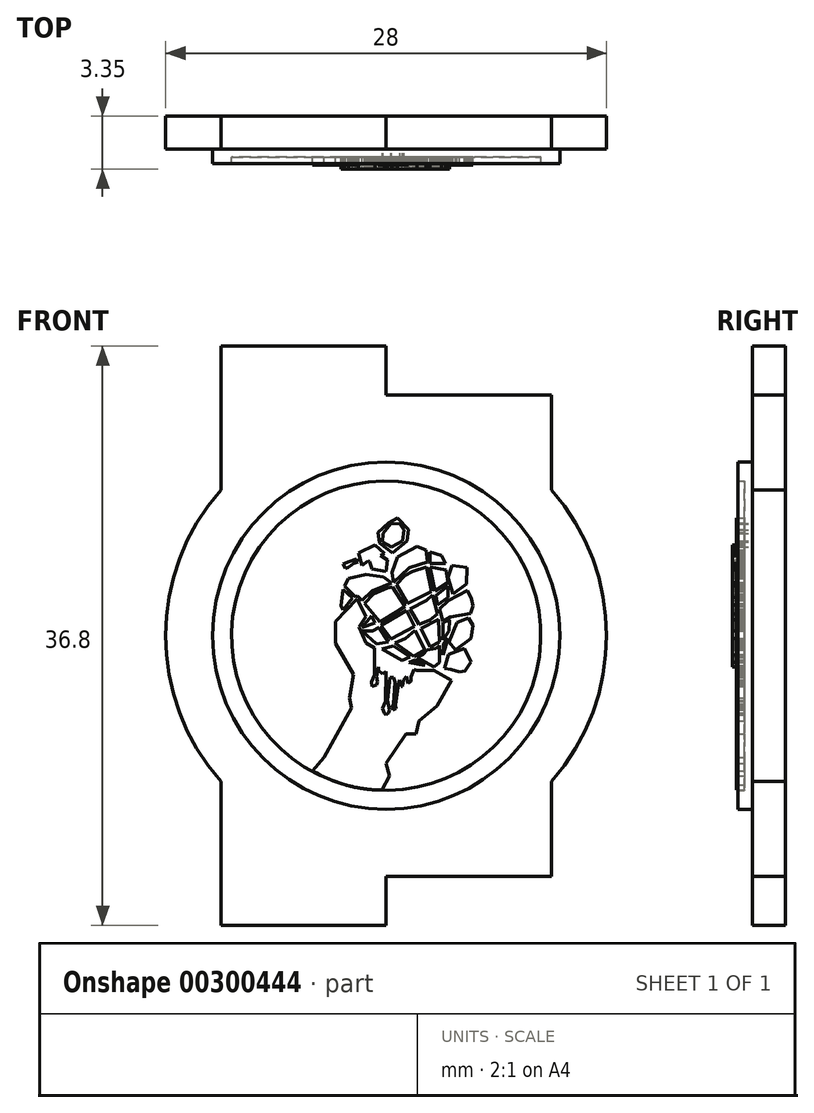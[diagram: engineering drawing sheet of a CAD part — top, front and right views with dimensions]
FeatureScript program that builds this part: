
annotation { "Feature Type Name" : "Feature", "Feature Type Description" : "" }
export const myFeature = defineFeature(function(context is Context, id is Id, definition is map)
    precondition{}
    {
        {
            var Q0;
            Q0=qCreatedBy(makeId("Front.planeOp"),FACE);
            var sketch = newSketch(context, id + "F0", { "sketchPlane" : qUnion([Q0])});
            skLineSegment(sketch, "E0", {"start": v(0, 0) * mm, "end": v(10.5, 0) * mm, "construction": true});
            skLineSegment(sketch, "E1", {"start": v(0, 0) * mm, "end": v(-10.5, 0) * mm, "construction": true});
            skLineSegment(sketch, "E2", {"start": v(0, 0) * mm, "end": v(0, -18.4) * mm, "construction": true});
            skLineSegment(sketch, "E3", {"start": v(0, 0) * mm, "end": v(0, 18.4) * mm, "construction": true});
            skArc(sketch, "E4", {"start": v(-10.5, 9.26) * mm, "mid": v(-14, 0) * mm, "end": v(-10.5, -9.26) * mm});
            skLineSegment(sketch, "E5", {"start": v(-10.5, 18.4) * mm, "end": v(-10.5, 9.26) * mm, "construction": true});
            skLineSegment(sketch, "E6.MirrorCS", {"start": v(10.5, 18.4) * mm, "end": v(10.5, -19.66) * mm, "construction": true});
            skLineSegment(sketch, "E7", {"start": v(0, 18.4) * mm, "end": v(-10.5, 18.4) * mm});
            skLineSegment(sketch, "E8", {"start": v(10.5, 0) * mm, "end": v(10.5, 15.3) * mm});
            skLineSegment(sketch, "E9", {"start": v(10.5, 15.3) * mm, "end": v(0, 15.3) * mm});
            skLineSegment(sketch, "E10", {"start": v(0, 15.3) * mm, "end": v(0, 18.4) * mm});
            skLineSegment(sketch, "E11", {"start": v(-10.5, 18.4) * mm, "end": v(-10.5, 9.26) * mm});
            skLineSegment(sketch, "E12.MirrorCS", {"start": v(-10.5, -18.4) * mm, "end": v(-10.5, -9.26) * mm});
            skLineSegment(sketch, "E13.MirrorCS", {"start": v(0, -18.4) * mm, "end": v(-10.5, -18.4) * mm});
            skLineSegment(sketch, "E14.MirrorCS", {"start": v(10.5, -15.3) * mm, "end": v(0, -15.3) * mm});
            skLineSegment(sketch, "E15.MirrorCS", {"start": v(10.5, -9.26) * mm, "end": v(10.5, -15.3) * mm});
            skPoint(sketch, "E16.orphan", {"position": v(-10.5, 0) * mm});
            skLineSegment(sketch, "E17.trimOffspring", {"start": v(-10.5, -9.26) * mm, "end": v(-10.5, -19.66) * mm, "construction": true});
            skPoint(sketch, "E18.orphan", {"position": v(10.5, 0) * mm});
            skArc(sketch, "E19.trimOffspring", {"start": v(10.5, -9.26) * mm, "mid": v(14, 0) * mm, "end": v(10.5, 9.26) * mm});
            skLineSegment(sketch, "E20", {"start": v(0, -15.3) * mm, "end": v(0, -18.4) * mm});
            skSolve(sketch);
        }
        {
            var Q0;
            Q0=makeQuery(id+"F0.imprint","IMPRINT",FACE,{"disambiguationData":[TD([[makeQuery(id+"F0.imprint","IMPRINT",EDGE,{"derivedFrom":sQuery(id+"F0.wireOp",EDGE,"E4")}),1.0]])]});
            var sketch = newSketch(context, id + "F1", { "sketchPlane" : qUnion([Q0])});
            skCircle(sketch, "E21", {"center": v(0, 0) * mm, "radius": 11.03 * mm});
            skCircle(sketch, "E22", {"center": v(0, 0) * mm, "radius": 9.82 * mm});
            skSolve(sketch);
        }
        {
            var Q0;
            Q0=makeQuery(id+"F0.imprint","IMPRINT",FACE,{"disambiguationData":[TD([[makeQuery(id+"F0.imprint","IMPRINT",EDGE,{"derivedFrom":sQuery(id+"F0.wireOp",EDGE,"E4")}),1.0]])]});
            extrude(context, id + "F2", {"entities" : qUnion([Q0]), "depth" : 2.1 * mm});
        }
        {
            var Q0;
            Q0 = qSketchRegion(id + "F1", true);
            extrude(context, id + "F3", {"entities" : qUnion([Q0]), "operationType" : NewBodyOperationType.ADD, "depth" : 3 * mm});
        }
        {
            var Q0;
            {var subQ0=sQuery(id+"F0.wireOp",EDGE,"E14.MirrorCS");var subQ1=sQuery(id+"F0.wireOp",EDGE,"E13.MirrorCS");var subQ2=sQuery(id+"F0.wireOp",EDGE,"E12.MirrorCS");var subQ3=sQuery(id+"F0.wireOp",EDGE,"E11");var subQ4=sQuery(id+"F0.wireOp",EDGE,"E10");var subQ5=sQuery(id+"F0.wireOp",EDGE,"E15.MirrorCS");var subQ6=sQuery(id+"F0.wireOp",EDGE,"E4");var subQ7=sQuery(id+"F0.wireOp",EDGE,"E9");var subQ8=sQuery(id+"F0.wireOp",EDGE,"E7");var subQ9=sQuery(id+"F0.wireOp",EDGE,"E8");var subQ10=sQuery(id+"F0.wireOp",EDGE,"E19.trimOffspring");var subQ11=sQuery(id+"F0.wireOp",EDGE,"E20");Q0=makeQuery(id+"F3.boolean.opBoolean","SPLIT",FACE,{"disambiguationData":[TD([makeQuery(id+"F2.opExtrude","SWEPT_FACE",FACE,{"disambiguationData":[OSD([subQ6])]})])],"derivedFrom":makeQuery(id+"F2.opExtrude","CAP_FACE",FACE,{"disambiguationData":[OSD([subQ6,subQ8,subQ9,subQ7,subQ4,subQ3,subQ2,subQ1,subQ0,subQ5,subQ10,subQ11])],"isStart":false})});}
            var sketch = newSketch(context, id + "F4", { "sketchPlane" : qUnion([Q0])});
            skLineSegment(sketch, "E23", {"start": v(-4.66, -8.58) * mm, "end": v(-3.94, -7.74) * mm});
            skLineSegment(sketch, "E24", {"start": v(-3.94, -7.74) * mm, "end": v(-2.2, -4.58) * mm});
            skLineSegment(sketch, "E25", {"start": v(-2.2, -4.58) * mm, "end": v(-2.34, -3.96) * mm});
            skLineSegment(sketch, "E26", {"start": v(-2.34, -3.96) * mm, "end": v(-2.07, -2.47) * mm});
            skLineSegment(sketch, "E27", {"start": v(-2.07, -2.47) * mm, "end": v(-3.23, -0.5) * mm});
            skLineSegment(sketch, "E28", {"start": v(-3.23, -0.5) * mm, "end": v(-3.23, 0.92) * mm});
            skLineSegment(sketch, "E29", {"start": v(-3.23, 0.92) * mm, "end": v(-1.84, 2.32) * mm});
            skLineSegment(sketch, "E30", {"start": v(-1.84, 2.32) * mm, "end": v(-1.27, 1.2) * mm});
            skLineSegment(sketch, "E31", {"start": v(-1.27, 1.2) * mm, "end": v(-1.72, 0.56) * mm});
            skLineSegment(sketch, "E32", {"start": v(-1.72, 0.56) * mm, "end": v(-1.29, -0.48) * mm});
            skLineSegment(sketch, "E33", {"start": v(-1.29, -0.48) * mm, "end": v(0.72, -1.63) * mm});
            skLineSegment(sketch, "E34", {"start": v(0.72, -1.63) * mm, "end": v(0.72, -2.33) * mm});
            skLineSegment(sketch, "E35", {"start": v(0.72, -2.33) * mm, "end": v(1.05, -1.92) * mm});
            skLineSegment(sketch, "E36", {"start": v(1.05, -1.92) * mm, "end": v(1.96, -2.21) * mm});
            skLineSegment(sketch, "E37", {"start": v(1.96, -2.21) * mm, "end": v(3.04, -2.21) * mm});
            skLineSegment(sketch, "E38", {"start": v(3.04, -2.21) * mm, "end": v(4.16, -2.85) * mm});
            skLineSegment(sketch, "E39", {"start": v(4.16, -2.85) * mm, "end": v(3.25, -4.47) * mm});
            skLineSegment(sketch, "E40", {"start": v(3.25, -4.47) * mm, "end": v(2.1, -5.42) * mm});
            skLineSegment(sketch, "E41", {"start": v(2.1, -5.42) * mm, "end": v(1.88, -6.23) * mm});
            skLineSegment(sketch, "E42", {"start": v(1.88, -6.23) * mm, "end": v(1.27, -6.23) * mm});
            skLineSegment(sketch, "E43", {"start": v(1.27, -6.23) * mm, "end": v(0, -8.11) * mm});
            skLineSegment(sketch, "E44", {"start": v(0, -8.11) * mm, "end": v(0.21, -8.92) * mm});
            skLineSegment(sketch, "E45", {"start": v(0.21, -8.92) * mm, "end": v(-0.25, -9.81) * mm});
            skArc(sketch, "E46", {"start": v(-4.66, -8.58) * mm, "mid": v(-2.54, -9.49) * mm, "end": v(-0.25, -9.81) * mm});
            skLineSegment(sketch, "E47", {"start": v(-3.23, 0.92) * mm, "end": v(-2.75, 2.95) * mm});
            skLineSegment(sketch, "E48", {"start": v(-2.75, 2.95) * mm, "end": v(-2.4, 3.64) * mm});
            skLineSegment(sketch, "E49", {"start": v(-2.4, 3.64) * mm, "end": v(-1.27, 3.89) * mm});
            skLineSegment(sketch, "E50", {"start": v(-1.27, 3.89) * mm, "end": v(-0.17, 3.73) * mm});
            skLineSegment(sketch, "E51", {"start": v(-0.17, 3.73) * mm, "end": v(0.35, 3.36) * mm});
            skLineSegment(sketch, "E52", {"start": v(0.35, 3.36) * mm, "end": v(-0.9, 2.86) * mm});
            skLineSegment(sketch, "E53", {"start": v(-0.9, 2.86) * mm, "end": v(-1.53, 2.23) * mm});
            skLineSegment(sketch, "E54", {"start": v(-1.53, 2.23) * mm, "end": v(-1.83, 2.53) * mm});
            skLineSegment(sketch, "E55", {"start": v(-1.83, 2.53) * mm, "end": v(-1.95, 2.47) * mm});
            skLineSegment(sketch, "E56", {"start": v(-1.95, 2.47) * mm, "end": v(-2.64, 3.16) * mm});
            skLineSegment(sketch, "E57", {"start": v(-2.75, 2.95) * mm, "end": v(-2.14, 2.4) * mm});
            skLineSegment(sketch, "E58", {"start": v(-2.14, 2.4) * mm, "end": v(-2.75, 1.64) * mm});
            skLineSegment(sketch, "E59", {"start": v(-2.75, 1.64) * mm, "end": v(-2.87, 1.89) * mm});
            skLineSegment(sketch, "E60", {"start": v(-2.87, 1.89) * mm, "end": v(-2.75, 2.95) * mm});
            skLineSegment(sketch, "E61", {"start": v(0.48, 3.4) * mm, "end": v(0.36, 4) * mm});
            skLineSegment(sketch, "E62", {"start": v(0.36, 4) * mm, "end": v(0.71, 5.02) * mm});
            skLineSegment(sketch, "E63", {"start": v(0.71, 5.02) * mm, "end": v(1.95, 5.65) * mm});
            skLineSegment(sketch, "E64", {"start": v(1.95, 5.65) * mm, "end": v(2.53, 5.43) * mm});
            skLineSegment(sketch, "E65", {"start": v(2.53, 5.43) * mm, "end": v(2.64, 4.69) * mm});
            skLineSegment(sketch, "E66", {"start": v(2.64, 4.69) * mm, "end": v(1.52, 4.34) * mm});
            skLineSegment(sketch, "E67", {"start": v(1.52, 4.34) * mm, "end": v(1.44, 4.3) * mm});
            skLineSegment(sketch, "E68", {"start": v(1.44, 4.3) * mm, "end": v(0.48, 3.4) * mm});
            skLineSegment(sketch, "E69", {"start": v(2.79, 5.32) * mm, "end": v(2.79, 4.6) * mm});
            skLineSegment(sketch, "E70", {"start": v(2.79, 4.6) * mm, "end": v(3.77, 4.6) * mm});
            skLineSegment(sketch, "E71", {"start": v(3.77, 4.6) * mm, "end": v(3.52, 5.08) * mm});
            skLineSegment(sketch, "E72", {"start": v(3.52, 5.08) * mm, "end": v(2.79, 5.32) * mm});
            skLineSegment(sketch, "E73", {"start": v(2.79, 4.37) * mm, "end": v(3.09, 2.83) * mm});
            skLineSegment(sketch, "E74", {"start": v(3.09, 2.83) * mm, "end": v(3.92, 3.4) * mm});
            skLineSegment(sketch, "E75", {"start": v(3.92, 3.4) * mm, "end": v(3.8, 4.18) * mm});
            skLineSegment(sketch, "E76", {"start": v(3.8, 4.18) * mm, "end": v(2.79, 4.37) * mm});
            skLineSegment(sketch, "E77", {"start": v(0.66, 3.25) * mm, "end": v(1.2, 3.83) * mm});
            skLineSegment(sketch, "E78", {"start": v(1.2, 3.83) * mm, "end": v(1.68, 4.08) * mm});
            skLineSegment(sketch, "E79", {"start": v(1.68, 4.08) * mm, "end": v(2.57, 4.37) * mm});
            skLineSegment(sketch, "E80", {"start": v(2.57, 4.37) * mm, "end": v(2.87, 2.82) * mm});
            skLineSegment(sketch, "E81", {"start": v(2.87, 2.82) * mm, "end": v(1.36, 2.04) * mm});
            skLineSegment(sketch, "E82", {"start": v(1.36, 2.04) * mm, "end": v(0.66, 3.25) * mm});
            skLineSegment(sketch, "E83", {"start": v(-1.37, 2.06) * mm, "end": v(-0.82, 2.65) * mm});
            skLineSegment(sketch, "E84", {"start": v(-0.82, 2.65) * mm, "end": v(0.07, 3.03) * mm});
            skLineSegment(sketch, "E85", {"start": v(0.07, 3.03) * mm, "end": v(0.41, 3.1) * mm});
            skLineSegment(sketch, "E86", {"start": v(0.41, 3.1) * mm, "end": v(1.2, 1.86) * mm});
            skLineSegment(sketch, "E87", {"start": v(1.2, 1.86) * mm, "end": v(0.66, 1.52) * mm});
            skLineSegment(sketch, "E88", {"start": v(0.66, 1.52) * mm, "end": v(-0.4, 0.88) * mm});
            skLineSegment(sketch, "E89", {"start": v(-0.4, 0.88) * mm, "end": v(-1.37, 2.06) * mm});
            skLineSegment(sketch, "E90", {"start": v(-1.53, 0.5) * mm, "end": v(-0.94, 1.25) * mm});
            skLineSegment(sketch, "E91", {"start": v(-0.94, 1.25) * mm, "end": v(-0.7, 0.8) * mm});
            skLineSegment(sketch, "E92", {"start": v(-0.7, 0.8) * mm, "end": v(-1.53, 0.5) * mm});
            skLineSegment(sketch, "E93", {"start": v(-0.61, -0.53) * mm, "end": v(0.16, -0.39) * mm});
            skLineSegment(sketch, "E94", {"start": v(0.16, -0.39) * mm, "end": v(-0.46, 0.5) * mm});
            skLineSegment(sketch, "E95", {"start": v(-0.46, 0.5) * mm, "end": v(-0.87, 0.3) * mm});
            skLineSegment(sketch, "E96", {"start": v(-0.87, 0.3) * mm, "end": v(-1.53, 0.3) * mm});
            skLineSegment(sketch, "E97", {"start": v(-1.53, 0.3) * mm, "end": v(-0.61, -0.53) * mm});
            skLineSegment(sketch, "E98", {"start": v(-0.32, 0.65) * mm, "end": v(0.3, -0.2) * mm});
            skLineSegment(sketch, "E99", {"start": v(0.3, -0.2) * mm, "end": v(1.8, 0.58) * mm});
            skLineSegment(sketch, "E100", {"start": v(1.8, 0.58) * mm, "end": v(1.28, 1.6) * mm});
            skLineSegment(sketch, "E101", {"start": v(1.28, 1.6) * mm, "end": v(-0.32, 0.65) * mm});
            skLineSegment(sketch, "E102", {"start": v(1.51, 1.68) * mm, "end": v(1.99, 1.93) * mm});
            skLineSegment(sketch, "E103", {"start": v(1.99, 1.93) * mm, "end": v(2.57, 2.23) * mm});
            skLineSegment(sketch, "E104", {"start": v(2.57, 2.23) * mm, "end": v(2.95, 2.59) * mm});
            skLineSegment(sketch, "E105", {"start": v(2.95, 2.59) * mm, "end": v(3.25, 1.39) * mm});
            skLineSegment(sketch, "E106", {"start": v(3.25, 1.39) * mm, "end": v(2.79, 1) * mm});
            skLineSegment(sketch, "E107", {"start": v(2.79, 1) * mm, "end": v(2.08, 0.7) * mm});
            skLineSegment(sketch, "E108", {"start": v(2.08, 0.7) * mm, "end": v(1.51, 1.68) * mm});
            skLineSegment(sketch, "E109", {"start": v(3.15, 2.56) * mm, "end": v(3.26, 1.96) * mm});
            skLineSegment(sketch, "E110", {"start": v(3.26, 1.96) * mm, "end": v(3.93, 2.44) * mm});
            skLineSegment(sketch, "E111", {"start": v(3.93, 2.44) * mm, "end": v(3.93, 3.17) * mm});
            skLineSegment(sketch, "E112", {"start": v(3.93, 3.17) * mm, "end": v(3.15, 2.56) * mm});
            skLineSegment(sketch, "E113", {"start": v(-0.28, -0.83) * mm, "end": v(0.48, -0.64) * mm});
            skLineSegment(sketch, "E114", {"start": v(0.48, -0.64) * mm, "end": v(1.51, -1.37) * mm});
            skLineSegment(sketch, "E115", {"start": v(1.51, -1.37) * mm, "end": v(1.01, -1.58) * mm});
            skLineSegment(sketch, "E116", {"start": v(1.01, -1.58) * mm, "end": v(-0.28, -0.83) * mm});
            skLineSegment(sketch, "E117", {"start": v(1.44, -1.7) * mm, "end": v(1.84, -1.54) * mm});
            skLineSegment(sketch, "E118", {"start": v(1.84, -1.54) * mm, "end": v(2.48, -1.9) * mm});
            skLineSegment(sketch, "E119", {"start": v(2.48, -1.9) * mm, "end": v(1.44, -1.7) * mm});
            skLineSegment(sketch, "E120", {"start": v(0.55, -0.47) * mm, "end": v(1.24, -0.18) * mm});
            skLineSegment(sketch, "E121", {"start": v(1.24, -0.18) * mm, "end": v(1.84, 0.32) * mm});
            skLineSegment(sketch, "E122", {"start": v(1.84, 0.32) * mm, "end": v(2.46, -0.9) * mm});
            skLineSegment(sketch, "E123", {"start": v(2.46, -0.9) * mm, "end": v(1.78, -1.32) * mm});
            skLineSegment(sketch, "E124", {"start": v(1.78, -1.32) * mm, "end": v(0.55, -0.47) * mm});
            skLineSegment(sketch, "E125", {"start": v(3.6, 0.83) * mm, "end": v(3.6, -0.27) * mm});
            skLineSegment(sketch, "E126", {"start": v(3.6, -0.27) * mm, "end": v(4, 0.3) * mm});
            skLineSegment(sketch, "E127", {"start": v(4, 0.3) * mm, "end": v(4.03, 1) * mm});
            skLineSegment(sketch, "E128", {"start": v(4.03, 1) * mm, "end": v(3.6, 0.83) * mm});
            skLineSegment(sketch, "E129", {"start": v(1.96, -1.4) * mm, "end": v(2.34, -1.2) * mm});
            skLineSegment(sketch, "E130", {"start": v(2.34, -1.2) * mm, "end": v(2.6, -0.9) * mm});
            skLineSegment(sketch, "E131", {"start": v(2.6, -0.9) * mm, "end": v(3.16, -0.8) * mm});
            skLineSegment(sketch, "E132", {"start": v(3.16, -0.8) * mm, "end": v(3.39, -0.62) * mm});
            skLineSegment(sketch, "E133", {"start": v(3.39, -0.62) * mm, "end": v(3.39, -1.7) * mm});
            skLineSegment(sketch, "E134", {"start": v(3.39, -1.7) * mm, "end": v(3.04, -2) * mm});
            skLineSegment(sketch, "E135", {"start": v(3.04, -2) * mm, "end": v(1.96, -1.4) * mm});
            skLineSegment(sketch, "E136", {"start": v(3.93, -0.19) * mm, "end": v(3.63, -0.5) * mm});
            skLineSegment(sketch, "E137", {"start": v(3.63, -0.5) * mm, "end": v(3.6, -1.23) * mm});
            skLineSegment(sketch, "E138", {"start": v(3.6, -1.23) * mm, "end": v(3.93, -0.19) * mm});
            skLineSegment(sketch, "E139", {"start": v(-1.76, 5.25) * mm, "end": v(-1.53, 4.45) * mm});
            skLineSegment(sketch, "E140", {"start": v(-1.53, 4.45) * mm, "end": v(-1.16, 4.76) * mm});
            skLineSegment(sketch, "E141", {"start": v(-1.16, 4.76) * mm, "end": v(-1.06, 4.72) * mm});
            skLineSegment(sketch, "E142", {"start": v(-1.06, 4.72) * mm, "end": v(-0.89, 4.25) * mm});
            skLineSegment(sketch, "E143", {"start": v(-0.89, 4.25) * mm, "end": v(0, 4.1) * mm});
            skLineSegment(sketch, "E144", {"start": v(0, 4.1) * mm, "end": v(0.07, 4.8) * mm});
            skLineSegment(sketch, "E145", {"start": v(0.07, 4.8) * mm, "end": v(-0.35, 5.1) * mm});
            skLineSegment(sketch, "E146", {"start": v(-0.35, 5.1) * mm, "end": v(-0.12, 5.21) * mm});
            skLineSegment(sketch, "E147", {"start": v(-0.12, 5.21) * mm, "end": v(-0.7, 5.76) * mm});
            skLineSegment(sketch, "E148", {"start": v(-0.7, 5.76) * mm, "end": v(-1.76, 5.25) * mm});
            skLineSegment(sketch, "E149", {"start": v(-2.75, 4.55) * mm, "end": v(-2.32, 4.7) * mm});
            skLineSegment(sketch, "E150", {"start": v(-2.32, 4.7) * mm, "end": v(-1.89, 4.88) * mm});
            skLineSegment(sketch, "E151", {"start": v(-1.89, 4.88) * mm, "end": v(-1.77, 4.7) * mm});
            skLineSegment(sketch, "E152", {"start": v(-1.77, 4.7) * mm, "end": v(-2.06, 4.6) * mm});
            skLineSegment(sketch, "E153", {"start": v(-2.06, 4.6) * mm, "end": v(-2.23, 4.45) * mm});
            skLineSegment(sketch, "E154", {"start": v(-2.23, 4.45) * mm, "end": v(-2.43, 4.33) * mm});
            skLineSegment(sketch, "E155", {"start": v(-2.43, 4.33) * mm, "end": v(-2.57, 4.26) * mm});
            skLineSegment(sketch, "E156", {"start": v(-2.57, 4.26) * mm, "end": v(-2.75, 4.55) * mm});
            skLineSegment(sketch, "E157", {"start": v(-0.52, 6.56) * mm, "end": v(0.14, 7.17) * mm});
            skLineSegment(sketch, "E158", {"start": v(0.14, 7.17) * mm, "end": v(0.72, 7.47) * mm});
            skLineSegment(sketch, "E159", {"start": v(0.72, 7.47) * mm, "end": v(1.42, 6.75) * mm});
            skLineSegment(sketch, "E160", {"start": v(1.42, 6.75) * mm, "end": v(1.3, 6.02) * mm});
            skLineSegment(sketch, "E161", {"start": v(1.3, 6.02) * mm, "end": v(0.39, 5.25) * mm});
            skLineSegment(sketch, "E162", {"start": v(0.39, 5.25) * mm, "end": v(-0.4, 5.88) * mm});
            skLineSegment(sketch, "E163", {"start": v(-0.4, 5.88) * mm, "end": v(-0.52, 6.56) * mm});
            skLineSegment(sketch, "E164", {"start": v(0.3, 7.13) * mm, "end": v(-0.2, 6.5) * mm});
            skLineSegment(sketch, "E165", {"start": v(-0.2, 6.5) * mm, "end": v(-0.24, 5.96) * mm});
            skLineSegment(sketch, "E166", {"start": v(-0.24, 5.96) * mm, "end": v(0.33, 5.64) * mm});
            skLineSegment(sketch, "E167", {"start": v(0.33, 5.64) * mm, "end": v(1.05, 6.01) * mm});
            skLineSegment(sketch, "E168", {"start": v(1.05, 6.01) * mm, "end": v(1.12, 6.7) * mm});
            skLineSegment(sketch, "E169", {"start": v(1.12, 6.7) * mm, "end": v(0.87, 7.1) * mm});
            skLineSegment(sketch, "E170", {"start": v(0.87, 7.1) * mm, "end": v(0.3, 7.13) * mm});
            skLineSegment(sketch, "E171", {"start": v(4.2, 4.46) * mm, "end": v(5.12, 4.33) * mm});
            skLineSegment(sketch, "E172", {"start": v(5.12, 4.33) * mm, "end": v(5.1, 3.29) * mm});
            skLineSegment(sketch, "E173", {"start": v(5.1, 3.29) * mm, "end": v(4.24, 2.65) * mm});
            skLineSegment(sketch, "E174", {"start": v(3.39, 1.68) * mm, "end": v(3.97, 2.23) * mm});
            skLineSegment(sketch, "E175", {"start": v(3.97, 2.23) * mm, "end": v(5.16, 2.86) * mm});
            skLineSegment(sketch, "E176", {"start": v(5.16, 2.86) * mm, "end": v(5.42, 2.33) * mm});
            skLineSegment(sketch, "E177", {"start": v(5.42, 2.33) * mm, "end": v(5.52, 1.89) * mm});
            skLineSegment(sketch, "E178", {"start": v(5.52, 1.89) * mm, "end": v(5.37, 1.4) * mm});
            skLineSegment(sketch, "E179", {"start": v(5.37, 1.4) * mm, "end": v(4.1, 1.18) * mm});
            skLineSegment(sketch, "E180", {"start": v(4.1, 1.18) * mm, "end": v(3.6, 0.92) * mm});
            skLineSegment(sketch, "E181", {"start": v(3.6, 0.92) * mm, "end": v(3.39, 1.68) * mm});
            skLineSegment(sketch, "E182", {"start": v(4, -0.4) * mm, "end": v(4.5, 0.83) * mm});
            skLineSegment(sketch, "E183", {"start": v(4.5, 0.83) * mm, "end": v(5.25, 1.13) * mm});
            skLineSegment(sketch, "E184", {"start": v(5.25, 1.13) * mm, "end": v(5.52, 0.64) * mm});
            skLineSegment(sketch, "E185", {"start": v(5.52, 0.64) * mm, "end": v(5.39, -0.19) * mm});
            skLineSegment(sketch, "E186", {"start": v(5.39, -0.19) * mm, "end": v(4.41, -0.9) * mm});
            skLineSegment(sketch, "E187", {"start": v(4.41, -0.9) * mm, "end": v(4, -0.4) * mm});
            skLineSegment(sketch, "E188", {"start": v(3.95, -1.2) * mm, "end": v(5, -0.82) * mm});
            skLineSegment(sketch, "E189", {"start": v(5, -0.82) * mm, "end": v(5.39, -1.66) * mm});
            skLineSegment(sketch, "E190", {"start": v(5.39, -1.66) * mm, "end": v(5, -2.25) * mm});
            skLineSegment(sketch, "E191", {"start": v(5, -2.25) * mm, "end": v(4.65, -2.3) * mm});
            skLineSegment(sketch, "E192", {"start": v(4.65, -2.3) * mm, "end": v(4.11, -2.16) * mm});
            skLineSegment(sketch, "E193", {"start": v(4.11, -2.16) * mm, "end": v(3.71, -2.09) * mm});
            skLineSegment(sketch, "E194", {"start": v(3.71, -2.09) * mm, "end": v(3.95, -1.2) * mm});
            skLineSegment(sketch, "E195", {"start": v(-0.75, -0.79) * mm, "end": v(-0.75, -2.5) * mm});
            skLineSegment(sketch, "E196", {"start": v(-0.75, -2.5) * mm, "end": v(-0.93, -2.95) * mm});
            skLineSegment(sketch, "E197", {"start": v(-0.93, -2.95) * mm, "end": v(-0.9, -3.22) * mm});
            skLineSegment(sketch, "E198", {"start": v(-0.9, -3.22) * mm, "end": v(-0.62, -3.13) * mm});
            skLineSegment(sketch, "E199", {"start": v(-0.62, -3.13) * mm, "end": v(-0.56, -2.93) * mm});
            skLineSegment(sketch, "E200", {"start": v(-0.56, -2.93) * mm, "end": v(-0.63, -2.6) * mm});
            skLineSegment(sketch, "E201", {"start": v(-0.63, -2.6) * mm, "end": v(-0.48, -2) * mm});
            skLineSegment(sketch, "E202", {"start": v(-0.48, -2) * mm, "end": v(-0.48, -2.21) * mm});
            skLineSegment(sketch, "E203", {"start": v(-0.48, -2.21) * mm, "end": v(-0.24, -2.44) * mm});
            skLineSegment(sketch, "E204", {"start": v(-0.24, -2.44) * mm, "end": v(0, -2.28) * mm});
            skLineSegment(sketch, "E205", {"start": v(0, -2.28) * mm, "end": v(-0.05, -4.18) * mm});
            skLineSegment(sketch, "E206", {"start": v(-0.05, -4.18) * mm, "end": v(-0.24, -4.63) * mm});
            skLineSegment(sketch, "E207", {"start": v(-0.24, -4.63) * mm, "end": v(-0.12, -4.95) * mm});
            skLineSegment(sketch, "E208", {"start": v(-0.12, -4.95) * mm, "end": v(0, -5.03) * mm});
            skLineSegment(sketch, "E209", {"start": v(0, -5.03) * mm, "end": v(0.16, -4.9) * mm});
            skLineSegment(sketch, "E210", {"start": v(0.16, -4.9) * mm, "end": v(0.22, -4.73) * mm});
            skLineSegment(sketch, "E211", {"start": v(0.22, -4.73) * mm, "end": v(0.1, -4.1) * mm});
            skLineSegment(sketch, "E212", {"start": v(0.1, -4.1) * mm, "end": v(0.24, -2.64) * mm});
            skLineSegment(sketch, "E213", {"start": v(0.24, -2.64) * mm, "end": v(0.46, -2.67) * mm});
            skLineSegment(sketch, "E214", {"start": v(0.46, -2.67) * mm, "end": v(0.55, -2.94) * mm});
            skLineSegment(sketch, "E215", {"start": v(0.55, -2.94) * mm, "end": v(0.47, -4.35) * mm});
            skLineSegment(sketch, "E216", {"start": v(0.47, -4.35) * mm, "end": v(0.41, -4.46) * mm});
            skLineSegment(sketch, "E217", {"start": v(0.41, -4.46) * mm, "end": v(0.42, -4.72) * mm});
            skLineSegment(sketch, "E218", {"start": v(0.42, -4.72) * mm, "end": v(0.62, -4.61) * mm});
            skLineSegment(sketch, "E219", {"start": v(0.62, -4.61) * mm, "end": v(0.6, -4.39) * mm});
            skLineSegment(sketch, "E220", {"start": v(0.6, -4.39) * mm, "end": v(0.77, -3.06) * mm});
            skLineSegment(sketch, "E221", {"start": v(0.77, -3.06) * mm, "end": v(0.84, -2.82) * mm});
            skLineSegment(sketch, "E222", {"start": v(0.84, -2.82) * mm, "end": v(0.94, -3.24) * mm});
            skLineSegment(sketch, "E223", {"start": v(0.94, -3.24) * mm, "end": v(1.05, -3.21) * mm});
            skLineSegment(sketch, "E224", {"start": v(1.05, -3.21) * mm, "end": v(1.11, -2.81) * mm});
            skLineSegment(sketch, "E225", {"start": v(1.11, -2.81) * mm, "end": v(1.28, -2.6) * mm});
            skLineSegment(sketch, "E226", {"start": v(1.28, -2.6) * mm, "end": v(1.4, -3.04) * mm});
            skLineSegment(sketch, "E227", {"start": v(1.4, -3.04) * mm, "end": v(1.57, -2.9) * mm});
            skLineSegment(sketch, "E228", {"start": v(1.57, -2.9) * mm, "end": v(1.57, -2.61) * mm});
            skLineSegment(sketch, "E229", {"start": v(1.57, -2.61) * mm, "end": v(1.77, -2.15) * mm});
            skLineSegment(sketch, "E230", {"start": v(1.77, -2.15) * mm, "end": v(1.05, -1.92) * mm});
            skLineSegment(sketch, "E231", {"start": v(-0.75, -0.79) * mm, "end": v(0.72, -1.63) * mm});
            skPoint(sketch, "E232.start.orphan", {"position": v(2.73, 0.65) * mm});
            skPoint(sketch, "E233.start.orphan", {"position": v(2.2, 0.5) * mm});
            skPoint(sketch, "E234.start.orphan", {"position": v(2.79, -0.72) * mm});
            skPoint(sketch, "E235.start.orphan", {"position": v(3.39, -0.4) * mm});
            skLineSegment(sketch, "E236", {"start": v(2.2, 0.46) * mm, "end": v(3.33, 1.04) * mm});
            skLineSegment(sketch, "E237", {"start": v(3.33, 1.04) * mm, "end": v(3.39, -0.4) * mm});
            skLineSegment(sketch, "E238", {"start": v(3.39, -0.4) * mm, "end": v(2.79, -0.72) * mm});
            skLineSegment(sketch, "E239", {"start": v(2.79, -0.72) * mm, "end": v(2.2, 0.46) * mm});
            skPoint(sketch, "E240.end.orphan", {"position": v(3.86, 3.79) * mm});
            skLineSegment(sketch, "E241", {"start": v(4.2, 4.46) * mm, "end": v(3.92, 3.7) * mm});
            skLineSegment(sketch, "E242", {"start": v(3.92, 3.7) * mm, "end": v(4.24, 2.65) * mm});
            skSolve(sketch);
        }
        {
            var Q0;
            Q0=makeQuery(id+"F4.imprint","IMPRINT",FACE,{"disambiguationData":[TD([[makeQuery(id+"F4.imprint","IMPRINT",EDGE,{"derivedFrom":sQuery(id+"F4.wireOp",EDGE,"E83")}),-1.0]])]});
            var Q1;
            Q1=makeQuery(id+"F4.imprint","IMPRINT",FACE,{"disambiguationData":[TD([[makeQuery(id+"F4.imprint","IMPRINT",EDGE,{"derivedFrom":sQuery(id+"F4.wireOp",EDGE,"E77")}),-1.0]])]});
            var Q2;
            Q2=makeQuery(id+"F4.imprint","IMPRINT",FACE,{"disambiguationData":[TD([[makeQuery(id+"F4.imprint","IMPRINT",EDGE,{"derivedFrom":sQuery(id+"F4.wireOp",EDGE,"E57")}),-1.0]])]});
            var Q3;
            {var subQ0=sQuery(id+"F4.wireOp",EDGE,"E49");Q3=makeQuery(id+"F4.imprint","IMPRINT",FACE,{"disambiguationData":[TD([[makeQuery(id+"F4.imprint","IMPRINT",EDGE,{"derivedFrom":subQ0}),-1.0]])]});}
            var Q4;
            Q4=makeQuery(id+"F4.imprint","IMPRINT",FACE,{"disambiguationData":[TD([[makeQuery(id+"F4.imprint","IMPRINT",EDGE,{"derivedFrom":sQuery(id+"F4.wireOp",EDGE,"E139")}),1.0]])]});
            var Q5;
            Q5=makeQuery(id+"F4.imprint","IMPRINT",FACE,{"disambiguationData":[TD([[makeQuery(id+"F4.imprint","IMPRINT",EDGE,{"derivedFrom":sQuery(id+"F4.wireOp",EDGE,"E69")}),1.0]])]});
            var Q6;
            Q6=makeQuery(id+"F4.imprint","IMPRINT",FACE,{"disambiguationData":[TD([[makeQuery(id+"F4.imprint","IMPRINT",EDGE,{"derivedFrom":sQuery(id+"F4.wireOp",EDGE,"E73")}),1.0]])]});
            var Q7;
            Q7=makeQuery(id+"F4.imprint","IMPRINT",FACE,{"disambiguationData":[TD([[makeQuery(id+"F4.imprint","IMPRINT",EDGE,{"derivedFrom":sQuery(id+"F4.wireOp",EDGE,"E93")}),1.0]])]});
            var Q8;
            Q8=makeQuery(id+"F4.imprint","IMPRINT",FACE,{"disambiguationData":[TD([[makeQuery(id+"F4.imprint","IMPRINT",EDGE,{"derivedFrom":sQuery(id+"F4.wireOp",EDGE,"E90")}),-1.0]])]});
            var Q9;
            Q9=makeQuery(id+"F4.imprint","IMPRINT",FACE,{"disambiguationData":[TD([[makeQuery(id+"F4.imprint","IMPRINT",EDGE,{"derivedFrom":sQuery(id+"F4.wireOp",EDGE,"E61")}),-1.0]])]});
            var Q10;
            Q10=makeQuery(id+"F4.imprint","IMPRINT",FACE,{"disambiguationData":[TD([[makeQuery(id+"F4.imprint","IMPRINT",EDGE,{"derivedFrom":sQuery(id+"F4.wireOp",EDGE,"E109")}),1.0]])]});
            var Q11;
            Q11=makeQuery(id+"F4.imprint","IMPRINT",FACE,{"disambiguationData":[TD([[makeQuery(id+"F4.imprint","IMPRINT",EDGE,{"derivedFrom":sQuery(id+"F4.wireOp",EDGE,"E125")}),1.0]])]});
            var Q12;
            Q12=makeQuery(id+"F4.imprint","IMPRINT",FACE,{"disambiguationData":[TD([[makeQuery(id+"F4.imprint","IMPRINT",EDGE,{"derivedFrom":sQuery(id+"F4.wireOp",EDGE,"E129")}),-1.0]])]});
            var Q13;
            Q13=makeQuery(id+"F4.imprint","IMPRINT",FACE,{"disambiguationData":[TD([[makeQuery(id+"F4.imprint","IMPRINT",EDGE,{"derivedFrom":sQuery(id+"F4.wireOp",EDGE,"E102")}),-1.0]])]});
            var Q14;
            Q14=makeQuery(id+"F4.imprint","IMPRINT",FACE,{"disambiguationData":[TD([[makeQuery(id+"F4.imprint","IMPRINT",EDGE,{"derivedFrom":sQuery(id+"F4.wireOp",EDGE,"E98")}),1.0]])]});
            var Q15;
            Q15=makeQuery(id+"F4.imprint","IMPRINT",FACE,{"disambiguationData":[TD([[makeQuery(id+"F4.imprint","IMPRINT",EDGE,{"derivedFrom":sQuery(id+"F4.wireOp",EDGE,"E120")}),-1.0]])]});
            var Q16;
            Q16=makeQuery(id+"F4.imprint","IMPRINT",FACE,{"disambiguationData":[TD([[makeQuery(id+"F4.imprint","IMPRINT",EDGE,{"derivedFrom":sQuery(id+"F4.wireOp",EDGE,"E113")}),-1.0]])]});
            var Q17;
            Q17=makeQuery(id+"F4.imprint","IMPRINT",FACE,{"disambiguationData":[TD([[makeQuery(id+"F4.imprint","IMPRINT",EDGE,{"derivedFrom":sQuery(id+"F4.wireOp",EDGE,"E117")}),-1.0]])]});
            var Q18;
            Q18=makeQuery(id+"F4.imprint","IMPRINT",FACE,{"disambiguationData":[TD([[makeQuery(id+"F4.imprint","IMPRINT",EDGE,{"derivedFrom":sQuery(id+"F4.wireOp",EDGE,"E136")}),1.0]])]});
            var Q19;
            Q19=makeQuery(id+"F4.imprint","IMPRINT",FACE,{"disambiguationData":[TD([[makeQuery(id+"F4.imprint","IMPRINT",EDGE,{"derivedFrom":sQuery(id+"F4.wireOp",EDGE,"E236")}),-1.0]])]});
            extrude(context, id + "F5", {"entities" : qUnion([Q0, Q1, Q2, Q3, Q4, Q5, Q6, Q7, Q8, Q9, Q10, Q11, Q12, Q13, Q14, Q15, Q16, Q17, Q18, Q19]), "operationType" : NewBodyOperationType.ADD, "depth" : 1.25 * mm});
        }
        {
            var Q0;
            Q0=makeQuery(id+"F4.imprint","IMPRINT",FACE,{"disambiguationData":[TD([[makeQuery(id+"F4.imprint","IMPRINT",EDGE,{"derivedFrom":sQuery(id+"F4.wireOp",EDGE,"E23")}),-1.0]])]});
            var Q1;
            Q1=makeQuery(id+"F4.imprint","IMPRINT",FACE,{"disambiguationData":[TD([[makeQuery(id+"F4.imprint","IMPRINT",EDGE,{"derivedFrom":sQuery(id+"F4.wireOp",EDGE,"E188")}),-1.0]])]});
            var Q2;
            Q2=makeQuery(id+"F4.imprint","IMPRINT",FACE,{"disambiguationData":[TD([[makeQuery(id+"F4.imprint","IMPRINT",EDGE,{"derivedFrom":sQuery(id+"F4.wireOp",EDGE,"E182")}),-1.0]])]});
            var Q3;
            Q3=makeQuery(id+"F4.imprint","IMPRINT",FACE,{"disambiguationData":[TD([[makeQuery(id+"F4.imprint","IMPRINT",EDGE,{"derivedFrom":sQuery(id+"F4.wireOp",EDGE,"E174")}),-1.0]])]});
            var Q4;
            Q4=makeQuery(id+"F4.imprint","IMPRINT",FACE,{"disambiguationData":[TD([[makeQuery(id+"F4.imprint","IMPRINT",EDGE,{"derivedFrom":sQuery(id+"F4.wireOp",EDGE,"w6QXty5G-VXHY-xHVT-cqj8-aE98eRItdoAz")}),-1.0]])]});
            var Q5;
            Q5=makeQuery(id+"F4.imprint","IMPRINT",FACE,{"disambiguationData":[TD([[makeQuery(id+"F4.imprint","IMPRINT",EDGE,{"derivedFrom":sQuery(id+"F4.wireOp",EDGE,"E157")}),-1.0]])]});
            var Q6;
            Q6=makeQuery(id+"F4.imprint","IMPRINT",FACE,{"disambiguationData":[TD([[makeQuery(id+"F4.imprint","IMPRINT",EDGE,{"derivedFrom":sQuery(id+"F4.wireOp",EDGE,"E149")}),-1.0]])]});
            extrude(context, id + "F6", {"entities" : qUnion([Q0, Q1, Q2, Q3, Q4, Q5, Q6]), "operationType" : NewBodyOperationType.ADD, "depth" : 1 * mm});
        }
        {
            var Q0;
            Q0=makeQuery(id+"F5.opExtrude","CAP_FACE",FACE,{"disambiguationData":[OSD([sQuery(id+"F0.wireOp",EDGE,"E4"),sQuery(id+"F0.wireOp",EDGE,"E7"),sQuery(id+"F0.wireOp",EDGE,"E8"),sQuery(id+"F0.wireOp",EDGE,"E9"),sQuery(id+"F0.wireOp",EDGE,"E10"),sQuery(id+"F0.wireOp",EDGE,"E11"),sQuery(id+"F0.wireOp",EDGE,"E12.MirrorCS"),sQuery(id+"F0.wireOp",EDGE,"E13.MirrorCS"),sQuery(id+"F0.wireOp",EDGE,"E14.MirrorCS"),sQuery(id+"F0.wireOp",EDGE,"E15.MirrorCS"),sQuery(id+"F0.wireOp",EDGE,"E19.trimOffspring"),sQuery(id+"F0.wireOp",EDGE,"E20"),sQuery(id+"F1.wireOp",EDGE,"E21"),sQuery(id+"F4.wireOp",EDGE,"E23"),sQuery(id+"F4.wireOp",EDGE,"E24"),sQuery(id+"F4.wireOp",EDGE,"E25"),sQuery(id+"F4.wireOp",EDGE,"E26"),sQuery(id+"F4.wireOp",EDGE,"E27"),sQuery(id+"F4.wireOp",EDGE,"E28"),sQuery(id+"F4.wireOp",EDGE,"E29"),sQuery(id+"F4.wireOp",EDGE,"E30"),sQuery(id+"F4.wireOp",EDGE,"E31"),sQuery(id+"F4.wireOp",EDGE,"E32"),sQuery(id+"F4.wireOp",EDGE,"E33"),sQuery(id+"F4.wireOp",EDGE,"E34"),sQuery(id+"F4.wireOp",EDGE,"E35"),sQuery(id+"F4.wireOp",EDGE,"E36"),sQuery(id+"F4.wireOp",EDGE,"E37"),sQuery(id+"F4.wireOp",EDGE,"E38"),sQuery(id+"F4.wireOp",EDGE,"E39"),sQuery(id+"F4.wireOp",EDGE,"E40"),sQuery(id+"F4.wireOp",EDGE,"E41"),sQuery(id+"F4.wireOp",EDGE,"E42"),sQuery(id+"F4.wireOp",EDGE,"E43"),sQuery(id+"F4.wireOp",EDGE,"E44"),sQuery(id+"F4.wireOp",EDGE,"E45"),sQuery(id+"F4.wireOp",EDGE,"E46"),sQuery(id+"F4.wireOp",EDGE,"E164"),sQuery(id+"F4.wireOp",EDGE,"E165"),sQuery(id+"F4.wireOp",EDGE,"E166"),sQuery(id+"F4.wireOp",EDGE,"E167"),sQuery(id+"F4.wireOp",EDGE,"E168"),sQuery(id+"F4.wireOp",EDGE,"E169"),sQuery(id+"F4.wireOp",EDGE,"E170"),sQuery(id+"F4.wireOp",EDGE,"w6QXty5G-VXHY-xHVT-cqj8-aE98eRItdoAz"),sQuery(id+"F4.wireOp",EDGE,"E171"),sQuery(id+"F4.wireOp",EDGE,"E172"),sQuery(id+"F4.wireOp",EDGE,"E173"),sQuery(id+"F4.wireOp",EDGE,"E240"),sQuery(id+"F4.wireOp",EDGE,"E174"),sQuery(id+"F4.wireOp",EDGE,"E175"),sQuery(id+"F4.wireOp",EDGE,"E176"),sQuery(id+"F4.wireOp",EDGE,"E177"),sQuery(id+"F4.wireOp",EDGE,"E178"),sQuery(id+"F4.wireOp",EDGE,"E179"),sQuery(id+"F4.wireOp",EDGE,"E180"),sQuery(id+"F4.wireOp",EDGE,"E181"),sQuery(id+"F4.wireOp",EDGE,"E182"),sQuery(id+"F4.wireOp",EDGE,"E183"),sQuery(id+"F4.wireOp",EDGE,"E184"),sQuery(id+"F4.wireOp",EDGE,"E185"),sQuery(id+"F4.wireOp",EDGE,"E186"),sQuery(id+"F4.wireOp",EDGE,"E187"),sQuery(id+"F4.wireOp",EDGE,"E188"),sQuery(id+"F4.wireOp",EDGE,"E189"),sQuery(id+"F4.wireOp",EDGE,"E190"),sQuery(id+"F4.wireOp",EDGE,"E191"),sQuery(id+"F4.wireOp",EDGE,"E192"),sQuery(id+"F4.wireOp",EDGE,"E193"),sQuery(id+"F4.wireOp",EDGE,"E194"),sQuery(id+"F4.wireOp",EDGE,"E230"),sQuery(id+"F4.wireOp",EDGE,"E231")])],"isStart":false});
            var Q1;
            Q1=makeQuery(id+"F4.imprint","IMPRINT",FACE,{"disambiguationData":[TD([[makeQuery(id+"F4.imprint","IMPRINT",EDGE,{"derivedFrom":sQuery(id+"F4.wireOp",EDGE,"E171")}),-1.0]])]});
            extrude(context, id + "F7", {"entities" : qUnion([Q0, Q1]), "operationType" : NewBodyOperationType.ADD, "depth" : 1 * mm});
        }
        {
            var Q0;
            {var subQ0=makeQuery(id+"F3.opExtrude","SWEPT_FACE",FACE,{"disambiguationData":[OSD([sQuery(id+"F1.wireOp",EDGE,"E22")])]});Q0=makeQuery(id+"F6.boolean.opBoolean","SPLIT",FACE,{"disambiguationData":[TD([subQ0])],"derivedFrom":makeQuery(id+"F3.boolean.opBoolean","SPLIT",FACE,{"disambiguationData":[TD([subQ0])],"derivedFrom":makeQuery(id+"F2.opExtrude","CAP_FACE",FACE,{"disambiguationData":[OSD([sQuery(id+"F0.wireOp",EDGE,"E4"),sQuery(id+"F0.wireOp",EDGE,"E7"),sQuery(id+"F0.wireOp",EDGE,"E8"),sQuery(id+"F0.wireOp",EDGE,"E9"),sQuery(id+"F0.wireOp",EDGE,"E10"),sQuery(id+"F0.wireOp",EDGE,"E11"),sQuery(id+"F0.wireOp",EDGE,"E12.MirrorCS"),sQuery(id+"F0.wireOp",EDGE,"E13.MirrorCS"),sQuery(id+"F0.wireOp",EDGE,"E14.MirrorCS"),sQuery(id+"F0.wireOp",EDGE,"E15.MirrorCS"),sQuery(id+"F0.wireOp",EDGE,"E19.trimOffspring"),sQuery(id+"F0.wireOp",EDGE,"E20")])],"isStart":false})})});}
            extrude(context, id + "F8", {"entities" : qUnion([Q0]), "operationType" : NewBodyOperationType.ADD, "depth" : 0.5 * mm});
        }
    });
